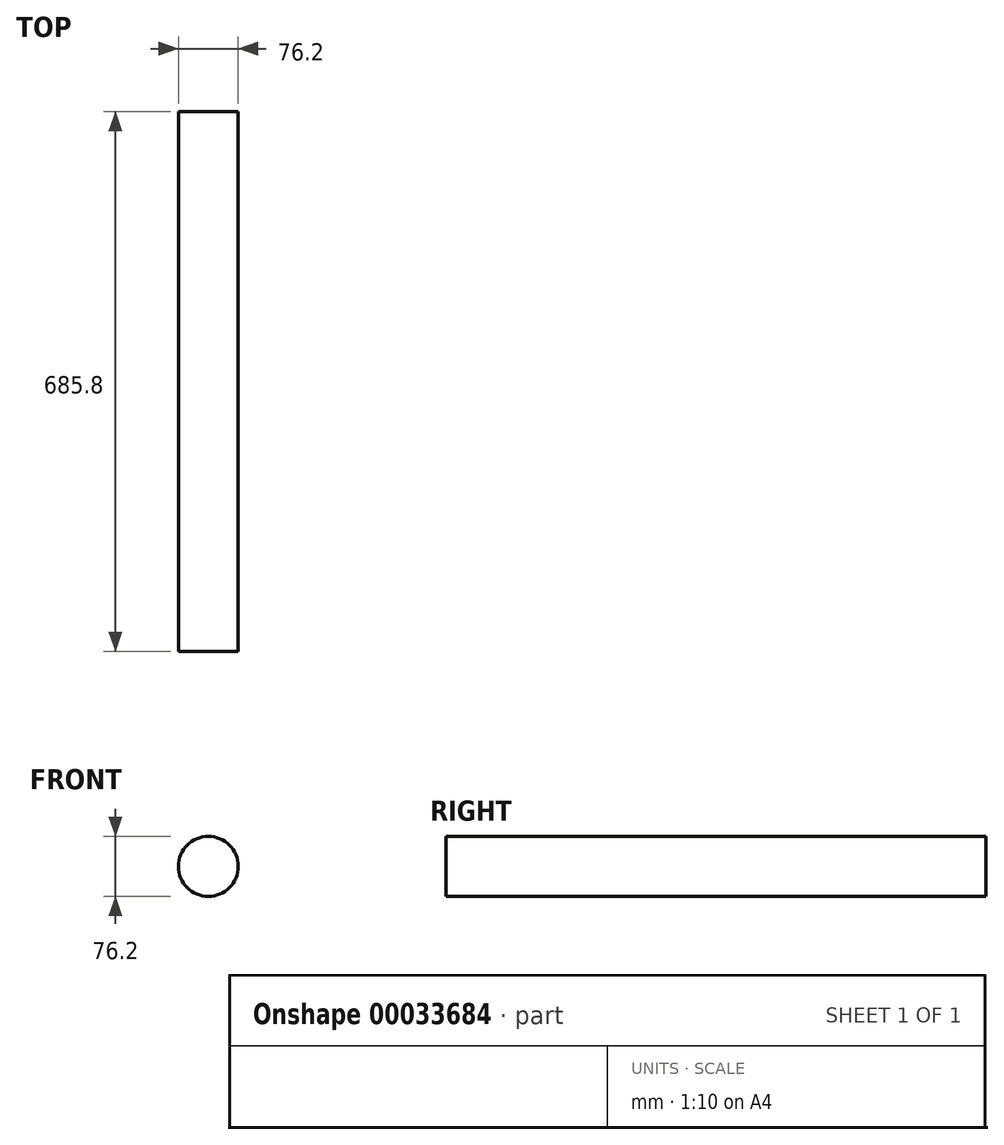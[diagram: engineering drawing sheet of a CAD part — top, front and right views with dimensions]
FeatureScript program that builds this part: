
annotation { "Feature Type Name" : "Feature", "Feature Type Description" : "" }
export const myFeature = defineFeature(function(context is Context, id is Id, definition is map)
    precondition{}
    {
        {
            var Q0;
            Q0=qCreatedBy(makeId("Front.planeOp"),FACE);
            var sketch = newSketch(context, id + "F0", { "sketchPlane" : qUnion([Q0])});
            skCircle(sketch, "E0", {"center": v(0, 0) * mm, "radius": 38.1 * mm});
            skSolve(sketch);
        }
        {
            var Q0;
            Q0 = qSketchRegion(id + "F0", true);
            extrude(context, id + "F1", {"entities" : qUnion([Q0]), "depth" : 685.8 * mm});
        }
    });
